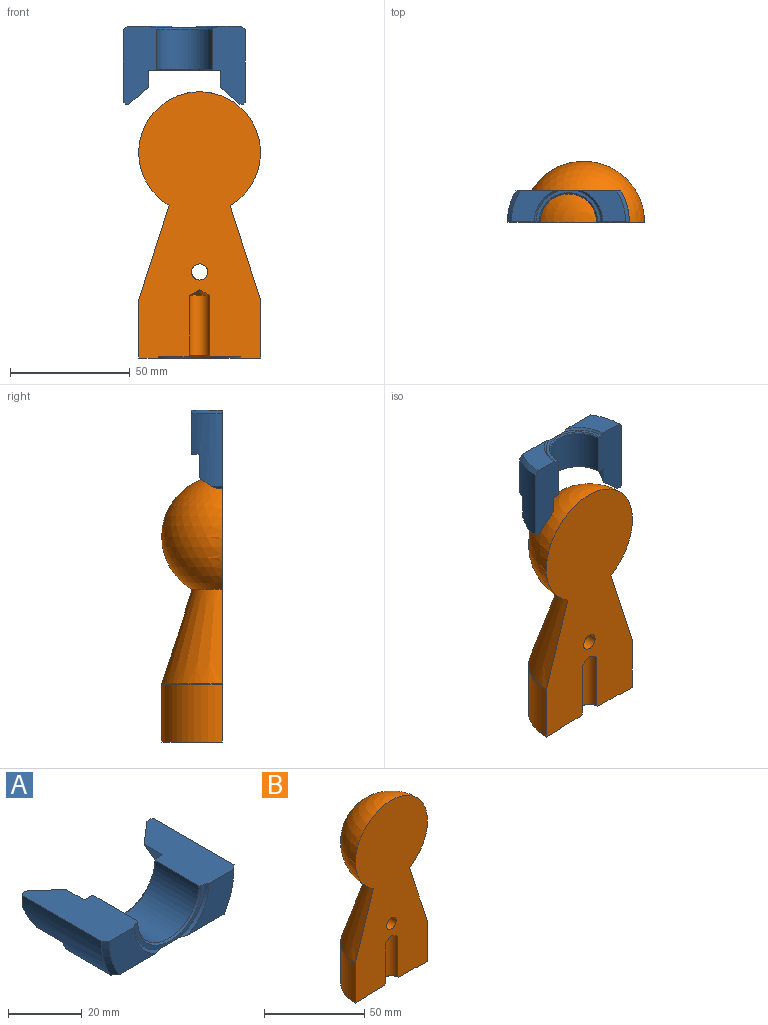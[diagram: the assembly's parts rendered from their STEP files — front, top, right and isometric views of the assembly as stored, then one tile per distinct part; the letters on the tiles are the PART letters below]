
ASSEMBLY  parts=2 mates=1
PART A: 26 faces, bbox 51x32.8x14 mm
  f0: plane 43.82x18.66mm, normal (0,0,-1), area 799.8mm2, adj f16,f17,f18,f19,f20,f21,f22,f23
  f1: plane 2.35x1.47mm, normal (0,1,0), area 1.8mm2, adj f6,f7,f13
  f2: plane 2.35x1.47mm, normal (0,1,0), area 1.8mm2, adj f4,f5,f15
  f3: cylinder r=11.71mm len=23.42mm, axis (0,-1,0), area 616.6mm2, adj f10,f13,f14,f15
  f4: cone r=0mm half-angle=45deg, axis (0,-1,0), area 3.8mm2, adj f2,f5,f15,f25
  f5: plane 10.19x9.7mm, normal (-0.61,0.71,-0.35), area 89.1mm2, adj f2,f4,f8,f9,f15,f25
  f6: plane 10.19x9.7mm, normal (0.61,0.71,-0.35), area 89.1mm2, adj f1,f7,f11,f12,f13,f24
  f7: cone r=0mm half-angle=45deg, axis (0,-1,0), area 3.8mm2, adj f1,f6,f13,f24
  f8: plane 9.66x3.09mm, normal (0,0,-1), area 25.7mm2, adj f5,f9,f16,f25
  f9: plane 9.53x6.99mm, normal (-0.87,0,-0.5), area 76.8mm2, adj f5,f8,f15,f16
  f10: cone r=0mm half-angle=45deg, axis (0,1,0), area 27mm2, adj f3,f13,f15,f16
  f11: plane 9.53x6.99mm, normal (0.87,0,-0.5), area 76.8mm2, adj f6,f12,f13,f16
  f12: plane 9.66x3.09mm, normal (0,0,-1), area 25.7mm2, adj f6,f11,f16,f24
  f13: plane 32.64x13.69mm, normal (0,0,1), area 368.5mm2, adj f1,f3,f6,f7,f10,f11,f14,f16
  f14: cone r=0mm half-angle=45deg, axis (0,-1,0), area 27mm2, adj f3,f13,f15,f17
  f15: plane 32.64x13.69mm, normal (0,0,1), area 368.5mm2, adj f2,f3,f4,f5,f9,f10,f14,f16
  f16: plane 47.09x12.95mm, normal (0,1,0), area 258.9mm2, adj f0,f8,f9,f10,f11,f12,f13,f15
  f17: plane 27.05x12.95mm, normal (0,-1,0), area 50mm2, adj f0,f13,f14,f15,f18,f19
  f18: cone r=0mm half-angle=45deg, axis (0,-1,0), area 18.1mm2, adj f0,f15,f17,f21
  f19: cone r=0mm half-angle=45deg, axis (0,-1,0), area 18.1mm2, adj f0,f13,f17,f20
  f20: plane 17.85x12.95mm, normal (0,-1,0), area 138.4mm2, adj f0,f13,f19,f22
  f21: plane 17.85x12.95mm, normal (0,-1,0), area 138.4mm2, adj f0,f15,f18,f23
  f22: cone r=0mm half-angle=45deg, axis (0,1,0), area 29.4mm2, adj f0,f13,f20,f24
  f23: cone r=0mm half-angle=45deg, axis (0,1,0), area 29.4mm2, adj f0,f15,f21,f25
  f24: cylinder r=25.4mm len=30.35mm, axis (0,-1,0), area 352.2mm2, adj f0,f6,f7,f12,f13,f16,f22
  f25: cylinder r=25.4mm len=30.35mm, axis (0,-1,0), area 352.2mm2, adj f0,f4,f5,f8,f15,f16,f23
PART B: 13 faces, bbox 55x27.5x111 mm
  f0: torus R=23.8mm, axis (0,0,1), area 39.7mm2, adj f8,f10,f12
  f1: cone r=17.14mm half-angle=45deg, axis (0,0,-1), area 36.3mm2, adj f6,f7,f12
  f2: cone r=4.17mm half-angle=45deg, axis (0,0,-1), area 12.6mm2, adj f4,f5,f12
  f3: cone r=0mm half-angle=59deg, axis (0,0,-1), area 31.8mm2, adj f4,f12
  f4: cylinder r=4.17mm len=24.93mm, axis (0,0,-1), area 326.2mm2, adj f2,f3,f12
  f5: plane 34.29x17.15mm, normal (0,0,-1), area 425.5mm2, adj f2,f6,f12
  f6: cylinder r=17.14mm len=34.29mm, axis (0,0,-1), area 2.1mm2, adj f1,f5,f12
  f7: plane 50.8x25.4mm, normal (0,0,-1), area 526mm2, adj f1,f8,f12
  f8: cylinder r=25.4mm len=50.8mm, axis (0,0,-1), area 1905.5mm2, adj f0,f7,f12
  f9: cylinder r=3.37mm len=22.7mm, axis (0,-1,0), area 454.4mm2, adj f10,f12
  f10: cone r=25.4mm half-angle=17.8deg, axis (0,0,-1), area 2424mm2, adj f0,f9,f11,f12
  f11: sphere r=25.4mm, area 3782.1mm2, adj f10,f12
  f12: plane 111x50.8mm, normal (0,-1,0), area 4421mm2, adj f0,f1,f2,f3,f4,f5,f6,f7
PLACE A rot(axis=(0,-0.71,0.71),180deg) t=(-6.34,0,138.43)mm
PLACE B at identity
MATE planar A.f15 <-> B.f12  axis (0,-1,0) through (-31.74,0,136.9)mm
